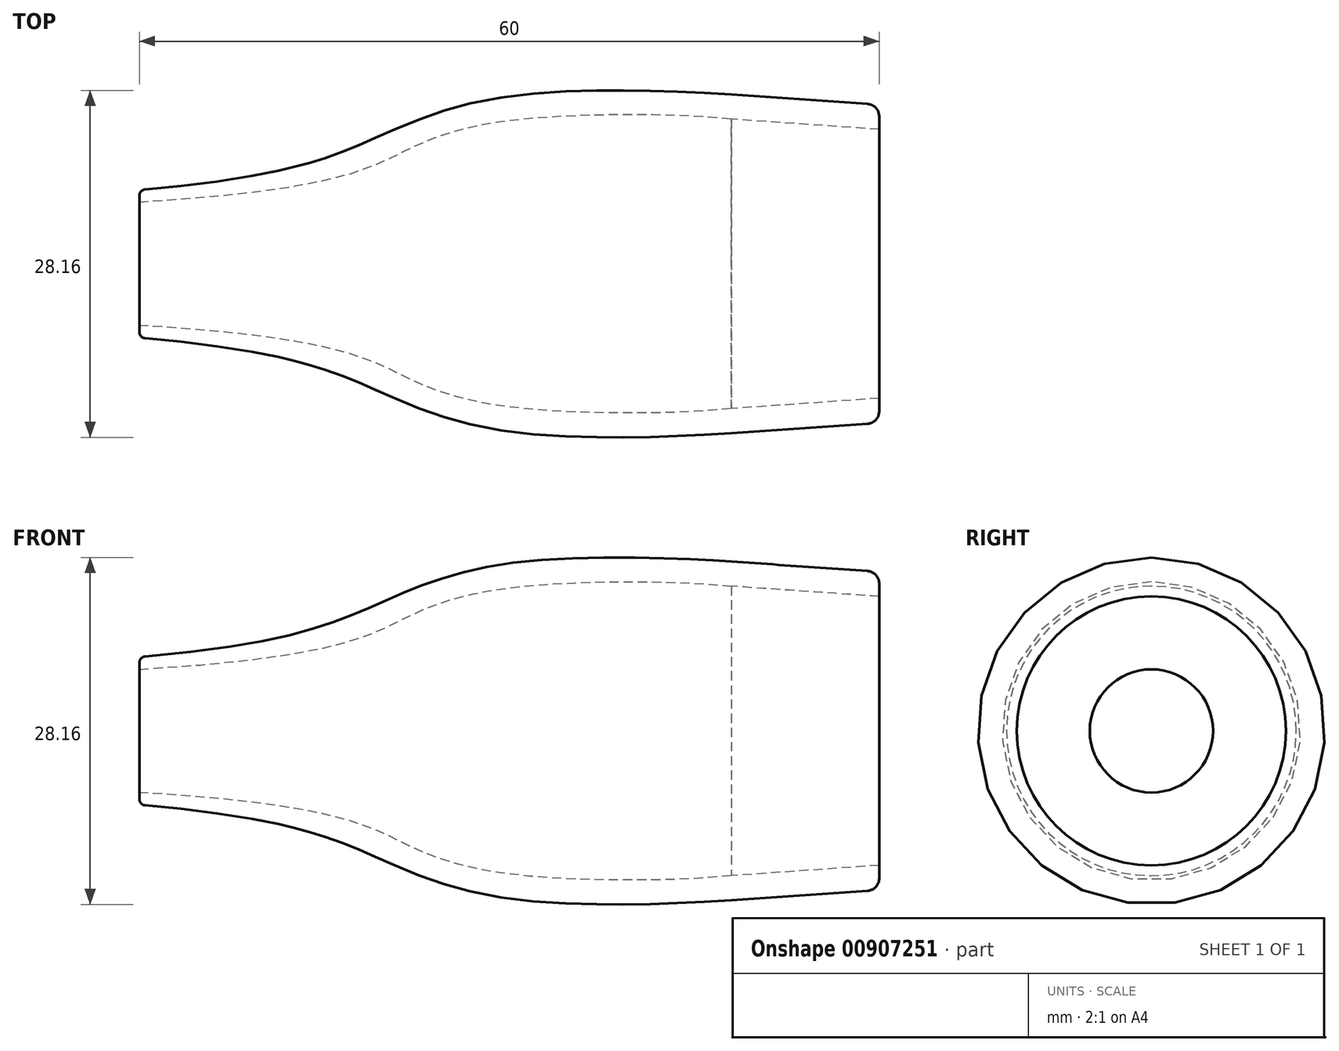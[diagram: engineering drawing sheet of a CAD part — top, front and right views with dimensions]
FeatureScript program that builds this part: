
annotation { "Feature Type Name" : "Feature", "Feature Type Description" : "" }
export const myFeature = defineFeature(function(context is Context, id is Id, definition is map)
    precondition{}
    {
        {
            var Q0;
            Q0=qCreatedBy(makeId("Front.planeOp"),FACE);
            var sketch = newSketch(context, id + "F0", { "sketchPlane" : qUnion([Q0])});
            skLineSegment(sketch, "E0", {"start": v(48, 13.75) * mm, "end": v(60, 12.91) * mm});
            skLineSegment(sketch, "E1", {"start": v(60, 12.91) * mm, "end": v(60, 10.91) * mm});
            skLineSegment(sketch, "E2", {"start": v(0, 6) * mm, "end": v(0, 5) * mm});
            skLineSegment(sketch, "E3", {"start": v(48, 11.75) * mm, "end": v(60, 10.91) * mm});
            skPoint(sketch, "E4.orphan", {"position": v(60, 0) * mm});
            skLineSegment(sketch, "E5", {"start": v(-2.44, 0) * mm, "end": v(52.34, 0) * mm, "construction": true});
            skFitSpline(sketch, "E6", {"points": [v(0, 6) * mm, v(19.12, 10.2) * mm, v(29.95, 13.6) * mm, v(48, 13.75) * mm], "startDerivative": vector(93.83, 8.05) * mm, "endDerivative": vector(28.53, -2) * mm});
            skFitSpline(sketch, "E7", {"points": [v(0, 5) * mm, v(22.13, 9.45) * mm, v(30.44, 11.67) * mm, v(48, 11.75) * mm], "startDerivative": vector(124.96, 7.45) * mm, "endDerivative": vector(28.59, -3.58) * mm});
            skSolve(sketch);
        }
        {
            var Q0;
            Q0 = qSketchRegion(id + "F0", true);
            var Q1;
            Q1=sQuery(id+"F0.wireOp",EDGE,"E5");
            revolve(context, id + "F1", {"surfaceOperationType" : NewSurfaceOperationType.NEW, "entities" : qUnion([Q0]), "axis" : qUnion([Q1]), "revolveType" : RevolveType.FULL});
        }
        {
            var Q0;
            Q0=makeQuery(id+"F1.opRevolve","SWEPT_EDGE",EDGE,{"disambiguationData":[OSD([sQuery(id+"F0.wireOp",EDGE,"E0"),sQuery(id+"F0.wireOp",EDGE,"E1")])]});
            fillet(context, id + "F2", {"entities" : qUnion([Q0]), "radius" : 1 * mm, "tangentPropagation" : true, "allowEdgeOverflow" : false});
        }
        {
            var Q0;
            Q0=makeQuery(id+"F1.opRevolve","SWEPT_EDGE",EDGE,{"disambiguationData":[OSD([sQuery(id+"F0.wireOp",EDGE,"E2"),sQuery(id+"F0.wireOp",EDGE,"E6")])]});
            fillet(context, id + "F3", {"entities" : qUnion([Q0]), "radius" : .5 * mm, "tangentPropagation" : true, "allowEdgeOverflow" : false});
        }
    });
